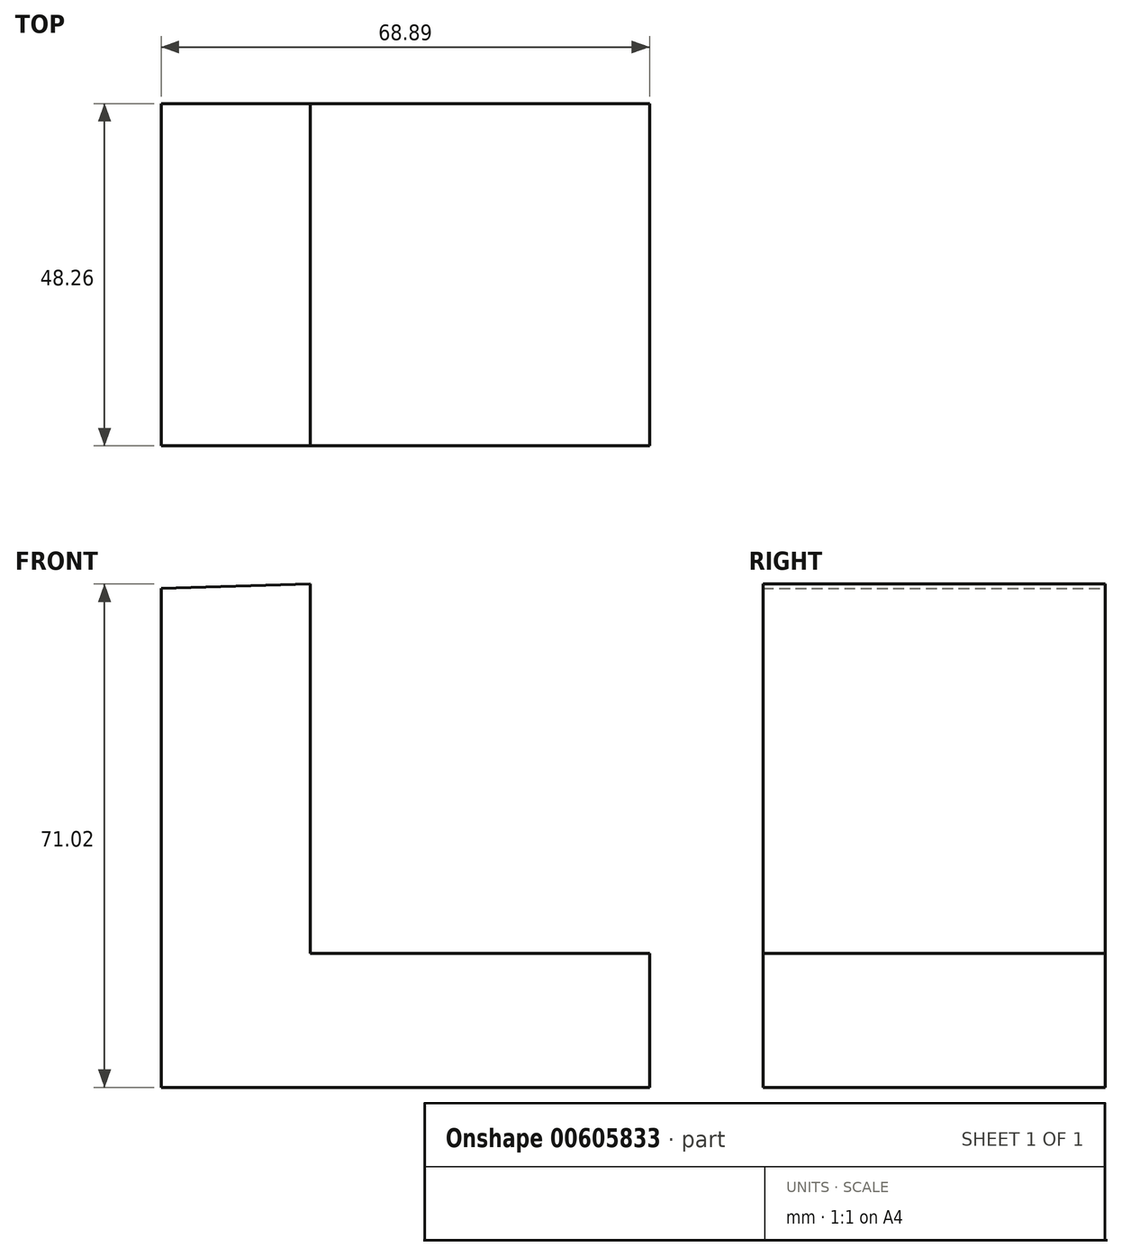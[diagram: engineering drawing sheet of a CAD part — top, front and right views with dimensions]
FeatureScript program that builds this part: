
annotation { "Feature Type Name" : "Feature", "Feature Type Description" : "" }
export const myFeature = defineFeature(function(context is Context, id is Id, definition is map)
    precondition{}
    {
        {
            var Q0;
            Q0=qCreatedBy(makeId("Front.planeOp"),FACE);
            var sketch = newSketch(context, id + "F0", { "sketchPlane" : qUnion([Q0])});
            skLineSegment(sketch, "E0", {"start": v(-36.12, 32.3) * mm, "end": v(-36.12, -38.1) * mm});
            skLineSegment(sketch, "E1", {"start": v(-36.12, -38.1) * mm, "end": v(32.77, -38.1) * mm});
            skLineSegment(sketch, "E2", {"start": v(32.77, -38.1) * mm, "end": v(32.77, -19.2) * mm});
            skLineSegment(sketch, "E3", {"start": v(32.77, -19.2) * mm, "end": v(-15.09, -19.2) * mm});
            skLineSegment(sketch, "E4", {"start": v(-15.09, -19.2) * mm, "end": v(-15.09, 32.92) * mm});
            skLineSegment(sketch, "E5", {"start": v(-15.09, 32.92) * mm, "end": v(-36.12, 32.3) * mm});
            skSolve(sketch);
        }
        {
            var Q0;
            Q0 = qSketchRegion(id + "F0", true);
            extrude(context, id + "F1", {"entities" : qUnion([Q0]), "depth" : 48.26 * mm, "offsetDistance" : 25.4 * mm});
        }
    });
